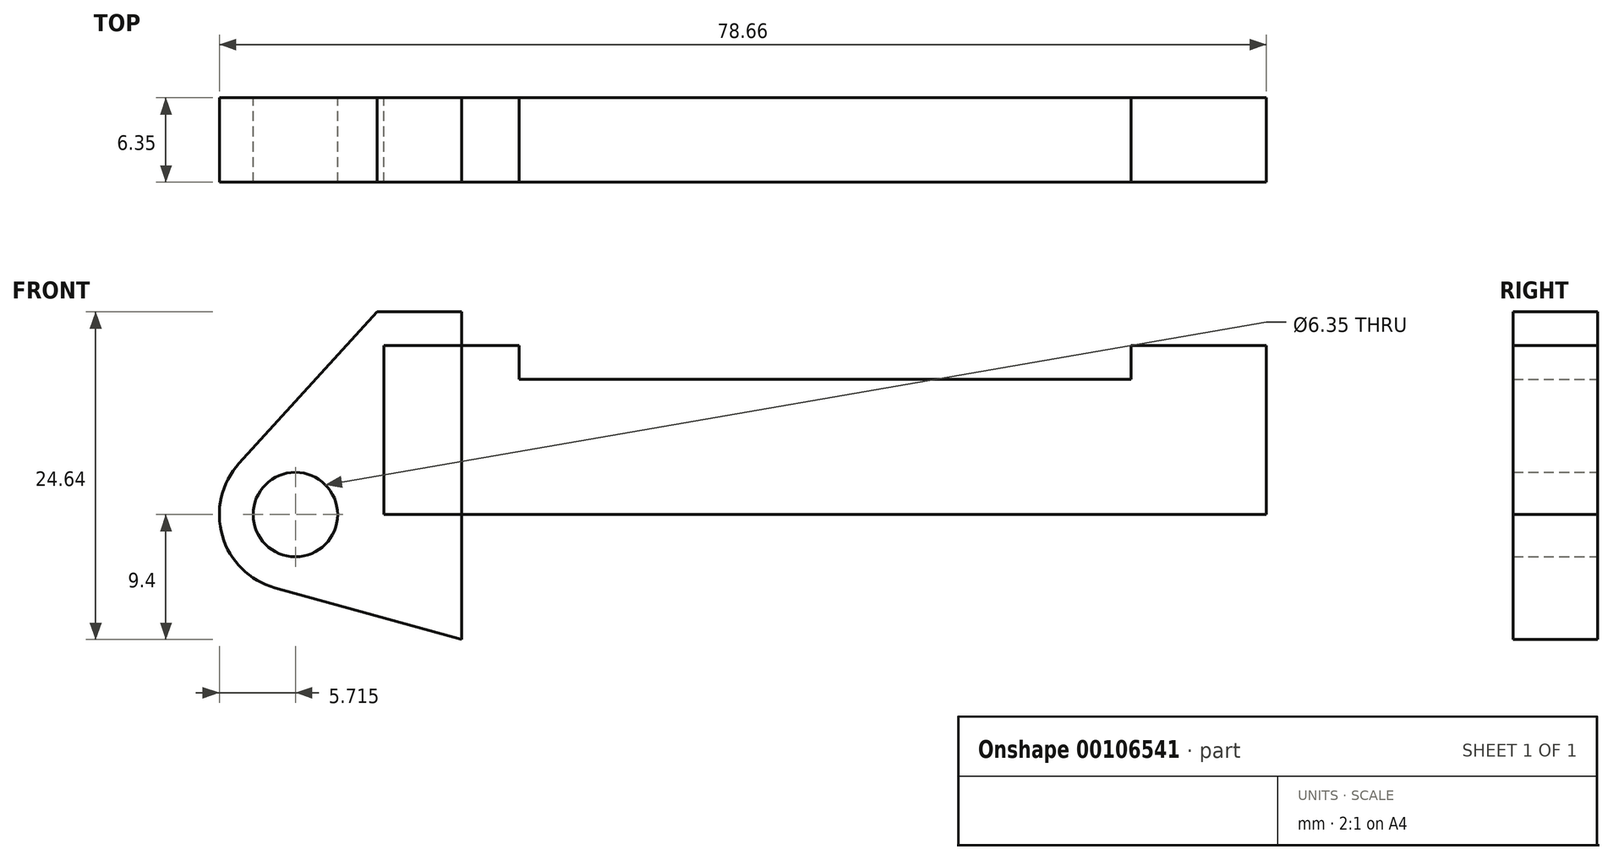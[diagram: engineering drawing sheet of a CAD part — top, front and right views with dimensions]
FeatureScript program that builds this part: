
annotation { "Feature Type Name" : "Feature", "Feature Type Description" : "" }
export const myFeature = defineFeature(function(context is Context, id is Id, definition is map)
    precondition{}
    {
        {
            var Q0;
            Q0=qCreatedBy(makeId("Front.planeOp"),FACE);
            var sketch = newSketch(context, id + "F0", { "sketchPlane" : qUnion([Q0])});
            skLineSegment(sketch, "E0", {"start": v(0, 0) * mm, "end": v(0, 12.7) * mm});
            skLineSegment(sketch, "E1", {"start": v(0, 12.7) * mm, "end": v(10.16, 12.7) * mm});
            skLineSegment(sketch, "E2", {"start": v(10.16, 12.7) * mm, "end": v(10.16, 10.16) * mm});
            skLineSegment(sketch, "E3", {"start": v(10.16, 10.16) * mm, "end": v(56.13, 10.16) * mm});
            skLineSegment(sketch, "E4", {"start": v(56.13, 10.16) * mm, "end": v(56.13, 12.7) * mm});
            skLineSegment(sketch, "E5", {"start": v(56.13, 12.7) * mm, "end": v(66.3, 12.7) * mm});
            skLineSegment(sketch, "E6", {"start": v(66.3, 12.7) * mm, "end": v(66.3, 0) * mm});
            skLineSegment(sketch, "E7", {"start": v(66.3, 0) * mm, "end": v(0, 0) * mm});
            skLineSegment(sketch, "E8", {"start": v(5.84, 15.24) * mm, "end": v(-0.5, 15.24) * mm});
            skLineSegment(sketch, "E9", {"start": v(-0.5, 15.24) * mm, "end": v(-10.88, 3.85) * mm});
            skLineSegment(sketch, "E10", {"start": v(0, 0) * mm, "end": v(-6.65, 0) * mm});
            skCircle(sketch, "E11", {"center": v(-6.65, 0) * mm, "radius": 5.72 * mm});
            skCircle(sketch, "E12", {"center": v(-6.65, 0) * mm, "radius": 3.18 * mm});
            skLineSegment(sketch, "E13", {"start": v(5.84, 15.24) * mm, "end": v(5.84, -9.4) * mm});
            skLineSegment(sketch, "E14", {"start": v(5.84, -9.4) * mm, "end": v(-8.18, -5.5) * mm});
            skSolve(sketch);
        }
        {
            var Q0;
            {var subQ3=sQuery(id+"F0.wireOp",EDGE,"E0");Q0=makeQuery(id+"F0.imprint","IMPRINT",FACE,{"disambiguationData":[TD([[makeQuery(id+"F0.imprint","IMPRINT",EDGE,{"derivedFrom":subQ3}),1.0]])]});}
            var Q1;
            {var subQ4=sQuery(id+"F0.wireOp",EDGE,"E12");Q1=makeQuery(id+"F0.imprint","IMPRINT",FACE,{"disambiguationData":[TD([[makeQuery(id+"F0.imprint","IMPRINT",EDGE,{"derivedFrom":subQ4}),-1.0]])]});}
            var Q2;
            {var subQ0=sQuery(id+"F0.wireOp",EDGE,"E14");Q2=makeQuery(id+"F0.imprint","IMPRINT",FACE,{"disambiguationData":[TD([[makeQuery(id+"F0.imprint","IMPRINT",EDGE,{"derivedFrom":subQ0}),-1.0]])]});}
            var Q3;
            {var subQ0=sQuery(id+"F0.wireOp",EDGE,"E2");Q3=makeQuery(id+"F0.imprint","IMPRINT",FACE,{"disambiguationData":[TD([[makeQuery(id+"F0.imprint","IMPRINT",EDGE,{"derivedFrom":subQ0}),-1.0]])]});}
            extrude(context, id + "F1", {"entities" : qUnion([Q0, Q1, Q2, Q3]), "depth" : 6.35 * mm});
        }
    });
